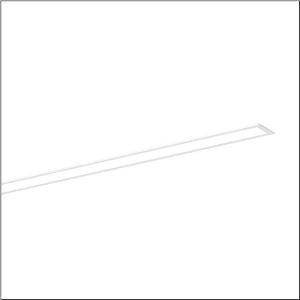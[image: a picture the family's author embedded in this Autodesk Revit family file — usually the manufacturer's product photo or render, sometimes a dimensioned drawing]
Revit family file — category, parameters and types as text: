
# Revit family: silica_r__21_51mx10da42wb_084b
name_source: partatom
category: Lighting Fixtures
units: mm (PartAtom-declared; Revit-internal decimal feet)

## family parameters
Cut with Voids When Loaded = No
Host = Face
Light Source = No
Part Type = Normal
Room Calculation Point = No
Round Connector Dimension = Use Diameter
Shared = No

## types (1)
- --- (1 x LED, 2400 lm, 15.2 W, 4000K)
    Apparent Load = 15 VA
    CIE Flux Codes = 48 79 96 100 100
    Color Rendering = 80
    Color Temperature = 4000K
    Default Elevation = 1800 mm
    Description = Silica® 21, office luminaire, primary optical cover: cover, of PMMA, opal, light emission: direct distribution, primary light characteristic: symmetric, installation type: recessed, LED, rated luminous flux: 2.400lm, luminous efficacy: 158lm/W, light colour: 840, colour temperature: 4000K, with terminal, 3+2-pole, max. 2.5mm², mains connection: 220..240V, AC, 50/60Hz, rated input power: 15.2W, luminaire housing, of aluminium, traffic white (RAL 9016), length: 1.228mm, width: 79mm, height: 53mm, protection rating (complete): IP20, insulation class (complete): insulation class I (protective earthing), certification: CE, permissible operating ambient temperature: 0..+35°C, standard: EN 50419, packaging unit: 1 piece
    Height = 0 mm  [stored 0 ft]
    Lamp = 1 x LED
    Lamp Light Flux = 2400 lm
    Lamp Power = 15.2 W
    Lamp count = 1
    Length = 1227 mm
    Luminous efficacy = 158 lm/W
    Manufacturer = Siteco
    ModVariant = No
    Model = 51MX10DA42WB
    Mounting Place = Ceiling
    Mounting Type = Recessed
    Number of Poles = 1
    OnlyDefault = Yes
    Power Factor = 1
    Product Name = Silica® 21
    Product group = office luminaire | ceiling recessed
    ProductGroupID = 401
    Protection Class = Protection class I
    Protection Degree = IP 20
    RLX_Detail_Level = 1
    RLX_Emergency_Light_Flux = 0 lm
    RLX_Emergency_Type = 0
    RLX_Emergency_Type_DB = No
    RlxData = <blob elided: 21001 chars, md5=888783c4>
    Socket = socket
    Standby Power = 0 W
    System Light Flux = 2400 lm
    System Power = 15 W
    Type Comments = factory setting: luminous flux: 100 % | dim-lin: 254 | 218 mA
    Type Image = l_1313615.jpg
    URL = http://relux.com
    VarID = @adj_065955
    Voltage = 0 V
    Weight = 0.00 kg
    Width = 79 mm

note: [stored X ft] marks values corroborated as IEEE doubles in the binary element streams (Revit-internal decimal feet)

## geometry (parser evidence)
native form markers: Blend x4, Sweep x11
no freeform markers — native parametric forms only
